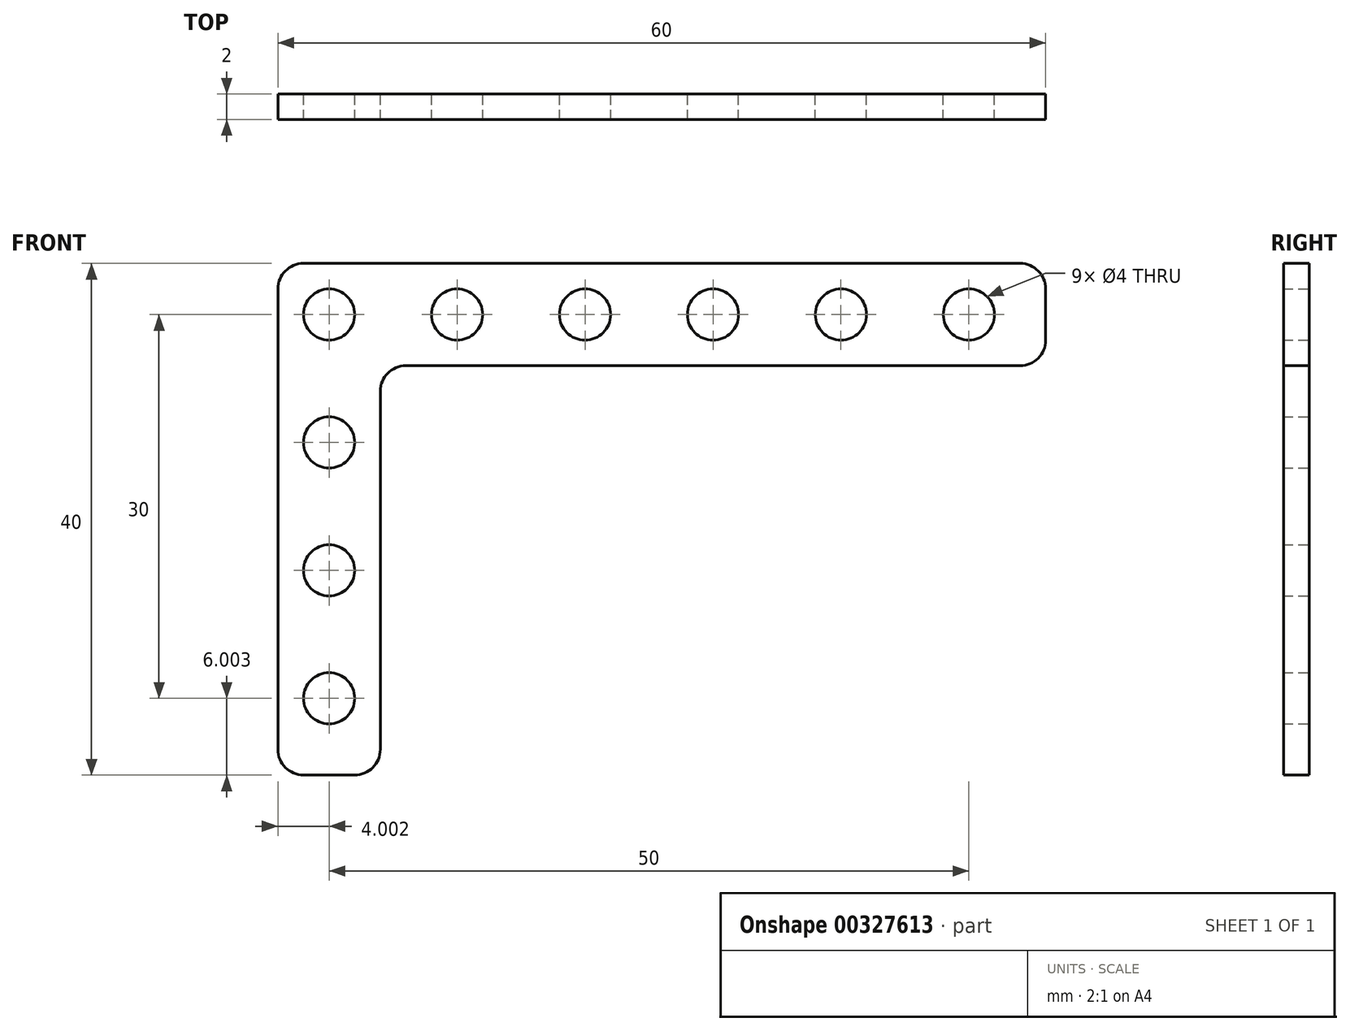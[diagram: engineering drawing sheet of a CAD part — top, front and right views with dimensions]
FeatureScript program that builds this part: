
annotation { "Feature Type Name" : "Feature", "Feature Type Description" : "" }
export const myFeature = defineFeature(function(context is Context, id is Id, definition is map)
    precondition{}
    {
        {
            var Q0;
            Q0=qCreatedBy(makeId("Front.planeOp"),FACE);
            var sketch = newSketch(context, id + "F0", { "sketchPlane" : qUnion([Q0])});
            skLineSegment(sketch, "E0", {"start": v(-17.04, -19.58) * mm, "end": v(-17.04, 20.42) * mm});
            skLineSegment(sketch, "E1", {"start": v(-17.04, 20.42) * mm, "end": v(42.96, 20.42) * mm});
            skLineSegment(sketch, "E2", {"start": v(42.96, 20.42) * mm, "end": v(42.96, 12.42) * mm});
            skLineSegment(sketch, "E3", {"start": v(42.96, 12.42) * mm, "end": v(-9.04, 12.42) * mm});
            skLineSegment(sketch, "E4", {"start": v(-9.04, 12.42) * mm, "end": v(-9.04, -19.58) * mm});
            skLineSegment(sketch, "E5", {"start": v(-9.04, -19.58) * mm, "end": v(-17.04, -19.58) * mm});
            skCircle(sketch, "E6", {"center": v(-13.04, 16.42) * mm, "radius": 2 * mm});
            skCircle(sketch, "E7.1.0.0", {"center": v(-3.04, 16.42) * mm, "radius": 2 * mm});
            skCircle(sketch, "E7.2.0.0", {"center": v(6.96, 16.42) * mm, "radius": 2 * mm});
            skCircle(sketch, "E7.3.0.0", {"center": v(16.96, 16.42) * mm, "radius": 2 * mm});
            skCircle(sketch, "E7.4.0.0", {"center": v(26.96, 16.42) * mm, "radius": 2 * mm});
            skCircle(sketch, "E7.5.0.0", {"center": v(36.96, 16.42) * mm, "radius": 2 * mm});
            skLineSegment(sketch, "E7.direction1", {"start": v(-13.04, 16.42) * mm, "end": v(-3.04, 16.42) * mm, "construction": true});
            skCircle(sketch, "E8.0.1.0", {"center": v(-13.04, 6.42) * mm, "radius": 2 * mm});
            skCircle(sketch, "E8.0.2.0", {"center": v(-13.04, -3.58) * mm, "radius": 2 * mm});
            skCircle(sketch, "E8.0.3.0", {"center": v(-13.04, -13.58) * mm, "radius": 2 * mm});
            skLineSegment(sketch, "E8.direction1", {"start": v(-13.04, 16.42) * mm, "end": v(11.96, 16.42) * mm, "construction": true});
            skLineSegment(sketch, "E8.direction2", {"start": v(-13.04, 16.42) * mm, "end": v(-13.04, 6.42) * mm, "construction": true});
            skSolve(sketch);
        }
        {
            var Q0;
            Q0=makeQuery(id+"F0.imprint","IMPRINT",FACE,{"disambiguationData":[TD([[makeQuery(id+"F0.imprint","IMPRINT",EDGE,{"derivedFrom":sQuery(id+"F0.wireOp",EDGE,"E0")}),-1.0]])]});
            extrude(context, id + "F1", {"entities" : qUnion([Q0]), "depth" : 2 * mm});
        }
        {
            var Q0;
            Q0=makeQuery(id+"F1.opExtrude","SWEPT_EDGE",EDGE,{"disambiguationData":[OSD([sQuery(id+"F0.wireOp",EDGE,"E0"),sQuery(id+"F0.wireOp",EDGE,"E1")])]});
            var Q1;
            Q1=makeQuery(id+"F1.opExtrude","SWEPT_EDGE",EDGE,{"disambiguationData":[OSD([sQuery(id+"F0.wireOp",EDGE,"E1"),sQuery(id+"F0.wireOp",EDGE,"E2")])]});
            var Q2;
            Q2=makeQuery(id+"F1.opExtrude","SWEPT_EDGE",EDGE,{"disambiguationData":[OSD([sQuery(id+"F0.wireOp",EDGE,"E2"),sQuery(id+"F0.wireOp",EDGE,"E3")])]});
            var Q3;
            Q3=makeQuery(id+"F1.opExtrude","SWEPT_EDGE",EDGE,{"disambiguationData":[OSD([sQuery(id+"F0.wireOp",EDGE,"E3"),sQuery(id+"F0.wireOp",EDGE,"E4")])]});
            var Q4;
            Q4=makeQuery(id+"F1.opExtrude","SWEPT_EDGE",EDGE,{"disambiguationData":[OSD([sQuery(id+"F0.wireOp",EDGE,"E4"),sQuery(id+"F0.wireOp",EDGE,"E5")])]});
            var Q5;
            Q5=makeQuery(id+"F1.opExtrude","SWEPT_EDGE",EDGE,{"disambiguationData":[OSD([sQuery(id+"F0.wireOp",EDGE,"E0"),sQuery(id+"F0.wireOp",EDGE,"E5")])]});
            fillet(context, id + "F2", {"entities" : qUnion([Q0, Q1, Q2, Q3, Q4, Q5]), "radius" : 2 * mm, "tangentPropagation" : true, "allowEdgeOverflow" : false});
        }
    });
